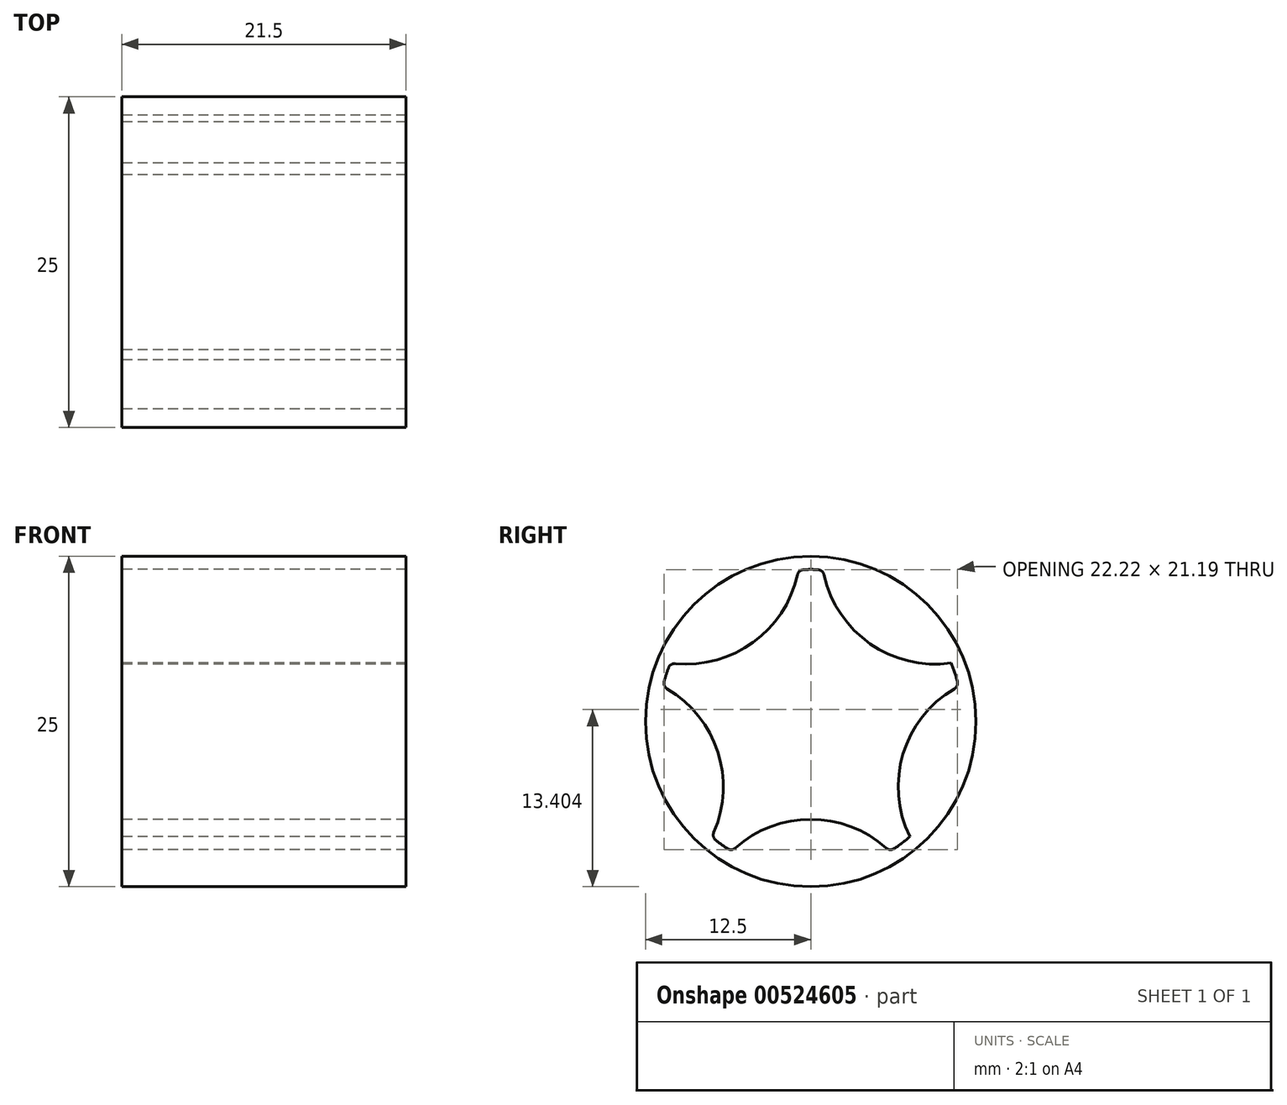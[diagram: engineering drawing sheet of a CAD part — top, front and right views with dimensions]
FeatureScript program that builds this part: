
annotation { "Feature Type Name" : "Feature", "Feature Type Description" : "" }
export const myFeature = defineFeature(function(context is Context, id is Id, definition is map)
    precondition{}
    {
        {
            var Q0;
            Q0=qCreatedBy(makeId("Right.planeOp"),FACE);
            var sketch = newSketch(context, id + "F0", { "sketchPlane" : qUnion([Q0])});
            skCircle(sketch, "E0", {"center": v(0, 0) * mm, "radius": 12.5 * mm});
            skArc(sketch, "E1", {"start": v(-10.61, 4.43) * mm, "mid": v(-10.94, 3.55) * mm, "end": v(-11.19, 2.65) * mm});
            skArc(sketch, "E2", {"start": v(5.98, -9.82) * mm, "mid": v(0, -7.4) * mm, "end": v(-5.98, -9.82) * mm});
            skArc(sketch, "E3.1.0", {"start": v(11.19, 2.65) * mm, "mid": v(7.04, -2.29) * mm, "end": v(7.5, -8.72) * mm});
            skArc(sketch, "E3.2.0", {"start": v(0.93, 11.46) * mm, "mid": v(4.35, 5.99) * mm, "end": v(10.61, 4.43) * mm});
            skArc(sketch, "E3.3.0", {"start": v(-10.61, 4.43) * mm, "mid": v(-4.35, 5.99) * mm, "end": v(-0.93, 11.46) * mm});
            skArc(sketch, "E3.4.0", {"start": v(-7.5, -8.72) * mm, "mid": v(-7.04, -2.29) * mm, "end": v(-11.19, 2.65) * mm});
            skLineSegment(sketch, "E4", {"start": v(0, 0) * mm, "end": v(0, -16) * mm, "construction": true});
            skArc(sketch, "E5.trimOffspring", {"start": v(-7.5, -8.72) * mm, "mid": v(-6.76, -9.3) * mm, "end": v(-5.98, -9.82) * mm});
            skArc(sketch, "E6.trimOffspring", {"start": v(5.98, -9.82) * mm, "mid": v(6.76, -9.3) * mm, "end": v(7.5, -8.72) * mm});
            skArc(sketch, "E7.trimOffspring", {"start": v(11.19, 2.65) * mm, "mid": v(10.94, 3.55) * mm, "end": v(10.61, 4.43) * mm});
            skArc(sketch, "E8.trimOffspring", {"start": v(0.93, 11.46) * mm, "mid": v(0, 11.5) * mm, "end": v(-0.93, 11.46) * mm});
            skSolve(sketch);
        }
        {
            var Q0;
            Q0 = qSketchRegion(id + "F0", true);
            extrude(context, id + "F1", {"entities" : qUnion([Q0]), "depth" : 21.5 * mm, "offsetDistance" : 25 * mm});
        }
        {
            var Q0;
            Q0=makeQuery(id+"F1.opExtrude","SWEPT_EDGE",EDGE,{"disambiguationData":[OSD([sQuery(id+"F0.wireOp",EDGE,"E3.3.0"),sQuery(id+"F0.wireOp",EDGE,"E8.trimOffspring")])]});
            var Q1;
            Q1=makeQuery(id+"F1.opExtrude","SWEPT_EDGE",EDGE,{"disambiguationData":[OSD([sQuery(id+"F0.wireOp",EDGE,"E3.2.0"),sQuery(id+"F0.wireOp",EDGE,"E8.trimOffspring")])]});
            var Q2;
            Q2=makeQuery(id+"F1.opExtrude","SWEPT_EDGE",EDGE,{"disambiguationData":[OSD([sQuery(id+"F0.wireOp",EDGE,"E1"),sQuery(id+"F0.wireOp",EDGE,"E3.3.0")])]});
            var Q3;
            Q3=makeQuery(id+"F1.opExtrude","SWEPT_EDGE",EDGE,{"disambiguationData":[OSD([sQuery(id+"F0.wireOp",EDGE,"E1"),sQuery(id+"F0.wireOp",EDGE,"E3.4.0")])]});
            var Q4;
            Q4=makeQuery(id+"F1.opExtrude","SWEPT_EDGE",EDGE,{"disambiguationData":[OSD([sQuery(id+"F0.wireOp",EDGE,"E3.4.0"),sQuery(id+"F0.wireOp",EDGE,"E5.trimOffspring")])]});
            var Q5;
            Q5=makeQuery(id+"F1.opExtrude","SWEPT_EDGE",EDGE,{"disambiguationData":[OSD([sQuery(id+"F0.wireOp",EDGE,"E2"),sQuery(id+"F0.wireOp",EDGE,"E5.trimOffspring")])]});
            var Q6;
            Q6=makeQuery(id+"F1.opExtrude","SWEPT_EDGE",EDGE,{"disambiguationData":[OSD([sQuery(id+"F0.wireOp",EDGE,"E2"),sQuery(id+"F0.wireOp",EDGE,"E6.trimOffspring")])]});
            var Q7;
            Q7=makeQuery(id+"F1.opExtrude","SWEPT_EDGE",EDGE,{"disambiguationData":[OSD([sQuery(id+"F0.wireOp",EDGE,"E3.1.0"),sQuery(id+"F0.wireOp",EDGE,"E7.trimOffspring")])]});
            fillet(context, id + "F2", {"entities" : qUnion([Q0, Q1, Q2, Q3, Q4, Q5, Q6, Q7]), "radius" : 0.5 * mm, "tangentPropagation" : true, "allowEdgeOverflow" : false});
        }
    });
